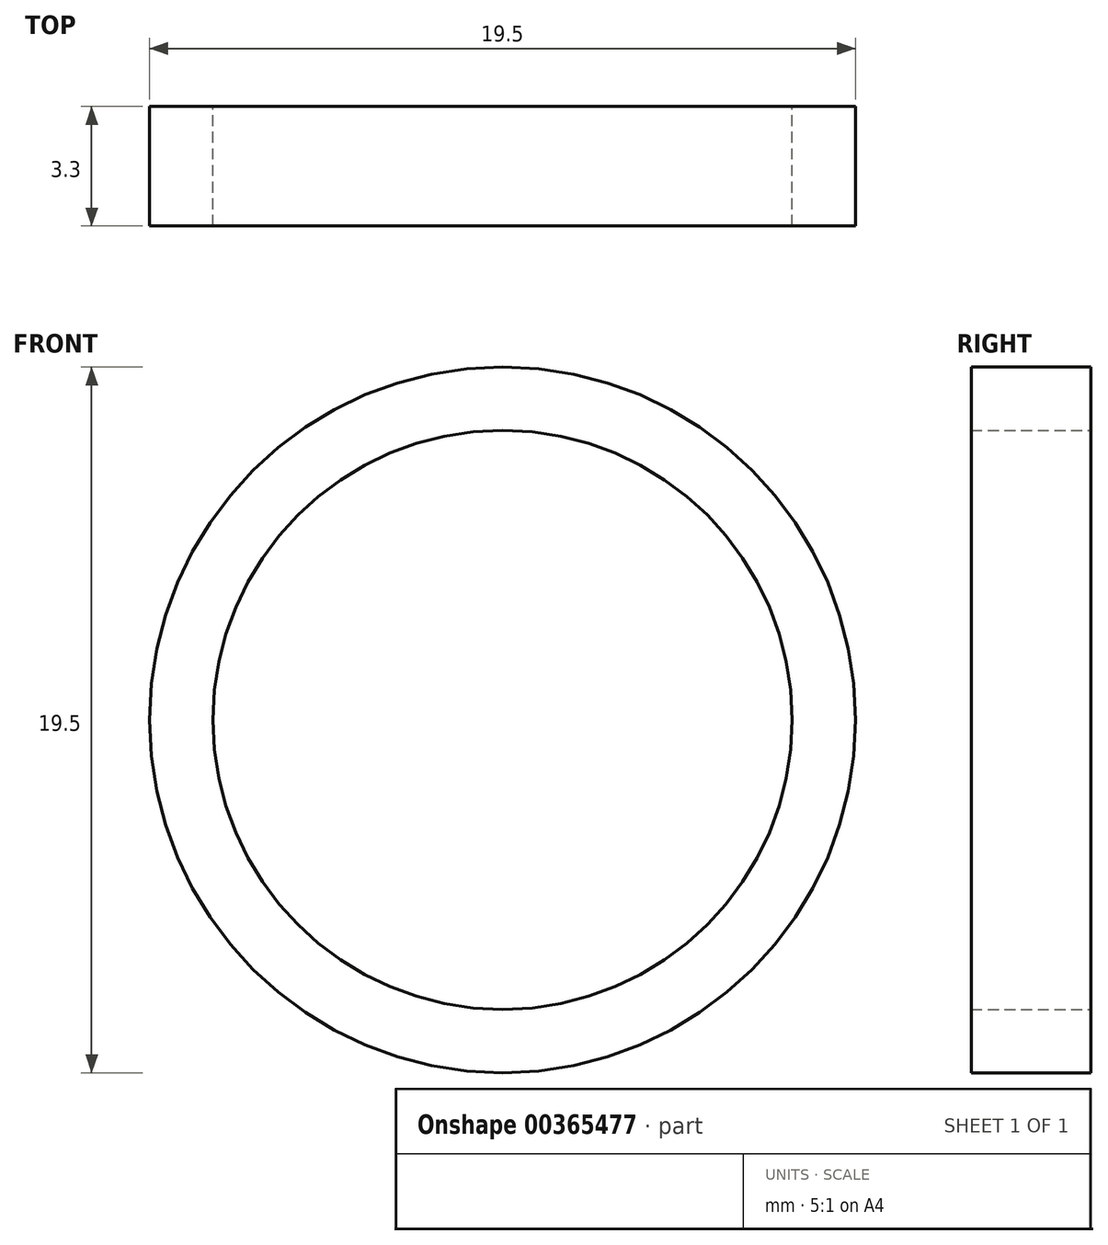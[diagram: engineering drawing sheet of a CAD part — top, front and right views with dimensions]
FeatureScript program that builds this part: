
annotation { "Feature Type Name" : "Feature", "Feature Type Description" : "" }
export const myFeature = defineFeature(function(context is Context, id is Id, definition is map)
    precondition{}
    {
        {
            var Q0;
            Q0=qCreatedBy(makeId("Front.planeOp"),FACE);
            var sketch = newSketch(context, id + "F0", { "sketchPlane" : qUnion([Q0])});
            skCircle(sketch, "E0", {"center": v(0, 0) * mm, "radius": 8 * mm});
            skCircle(sketch, "E1", {"center": v(0, 0) * mm, "radius": 9.75 * mm});
            skSolve(sketch);
        }
        {
            var Q0;
            Q0 = qSketchRegion(id + "F0", true);
            extrude(context, id + "F1", {"entities" : qUnion([Q0]), "depth" : 3.3 * mm});
        }
    });
